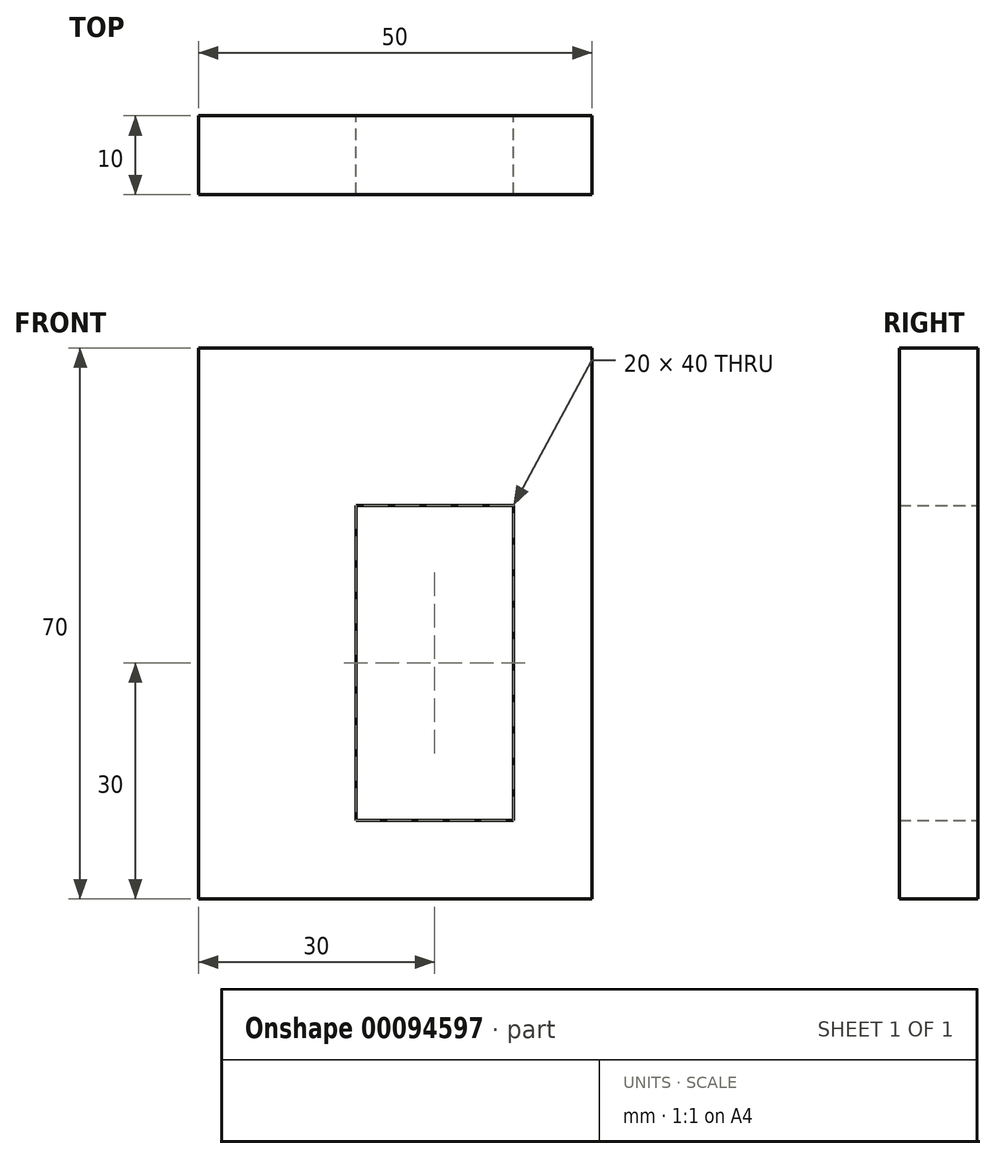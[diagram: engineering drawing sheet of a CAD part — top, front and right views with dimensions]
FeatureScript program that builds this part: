
annotation { "Feature Type Name" : "Feature", "Feature Type Description" : "" }
export const myFeature = defineFeature(function(context is Context, id is Id, definition is map)
    precondition{}
    {
        {
            var Q0;
            Q0=qCreatedBy(makeId("Front.planeOp"),FACE);
            var sketch = newSketch(context, id + "F0", { "sketchPlane" : qUnion([Q0])});
            skLineSegment(sketch, "E0", {"start": v(0, 0) * mm, "end": v(0, 70) * mm});
            skLineSegment(sketch, "E1", {"start": v(0, 70) * mm, "end": v(50, 70) * mm});
            skLineSegment(sketch, "E2", {"start": v(50, 70) * mm, "end": v(50, 0) * mm});
            skLineSegment(sketch, "E3", {"start": v(50, 0) * mm, "end": v(0, 0) * mm});
            skLineSegment(sketch, "E4", {"start": v(40, 10) * mm, "end": v(20, 10) * mm});
            skLineSegment(sketch, "E5", {"start": v(40, 10) * mm, "end": v(40, 50) * mm});
            skLineSegment(sketch, "E6", {"start": v(20, 10) * mm, "end": v(20, 50) * mm});
            skLineSegment(sketch, "E7", {"start": v(20, 50) * mm, "end": v(40, 50) * mm});
            skSolve(sketch);
        }
        {
            var Q0;
            Q0=makeQuery(id+"F0.imprint","IMPRINT",FACE,{"disambiguationData":[TD([[makeQuery(id+"F0.imprint","IMPRINT",EDGE,{"derivedFrom":sQuery(id+"F0.wireOp",EDGE,"E0")}),-1.0]])]});
            extrude(context, id + "F1", {"entities" : qUnion([Q0]), "depth" : 10 * mm});
        }
    });
